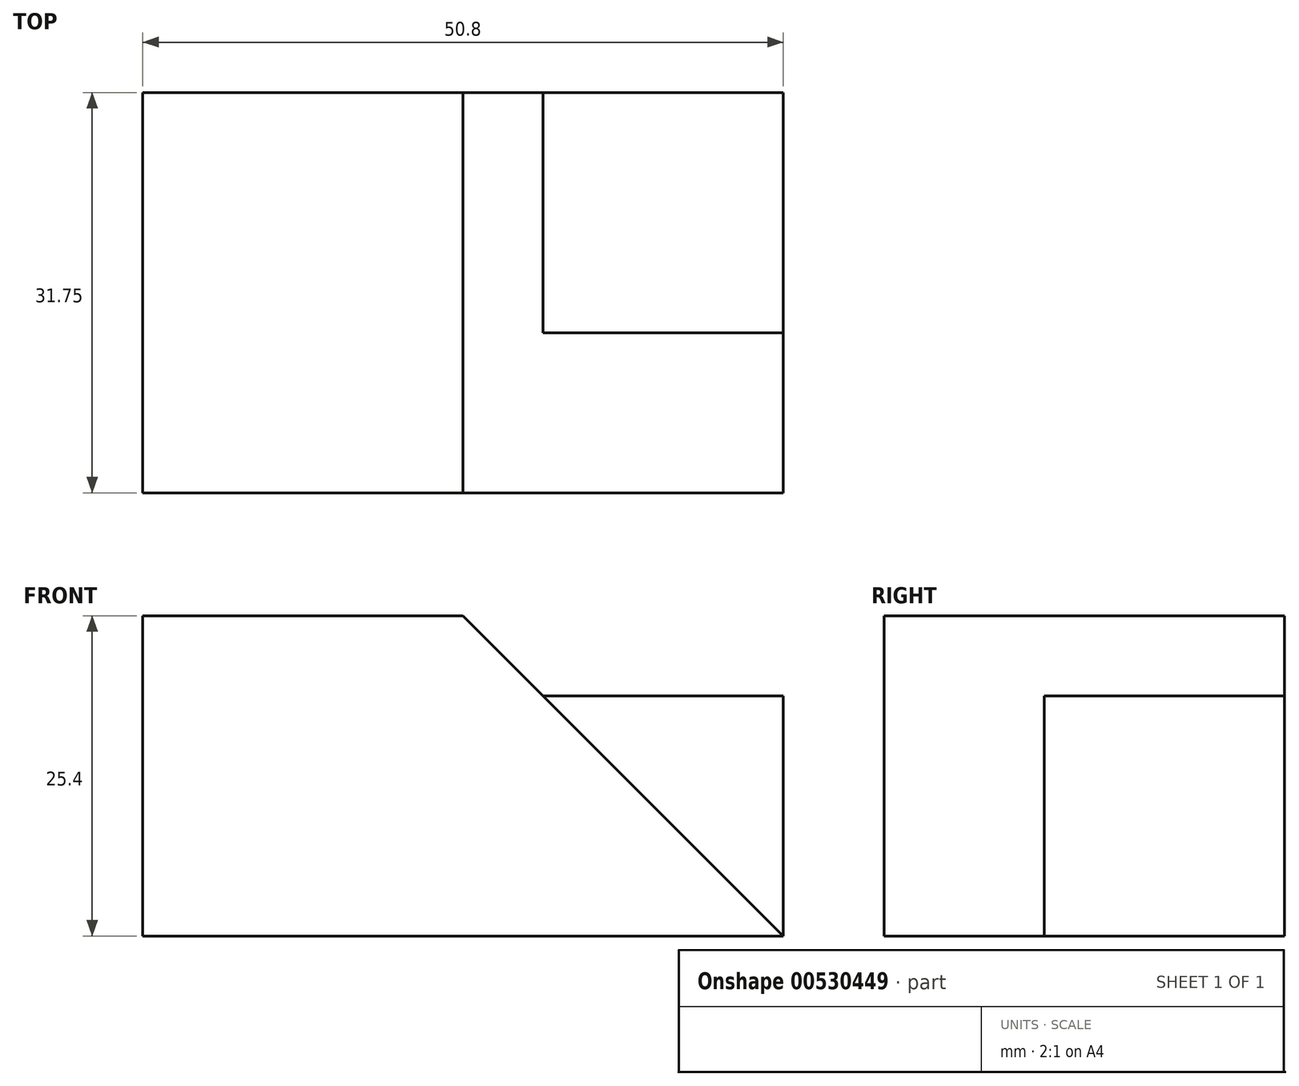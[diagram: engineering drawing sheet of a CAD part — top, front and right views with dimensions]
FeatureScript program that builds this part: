
annotation { "Feature Type Name" : "Feature", "Feature Type Description" : "" }
export const myFeature = defineFeature(function(context is Context, id is Id, definition is map)
    precondition{}
    {
        {
            var Q0;
            Q0=qCreatedBy(makeId("Front.planeOp"),FACE);
            var sketch = newSketch(context, id + "F0", { "sketchPlane" : qUnion([Q0])});
            skLineSegment(sketch, "E0", {"start": v(-56.42, 44.76) * mm, "end": v(-56.42, 19.36) * mm});
            skLineSegment(sketch, "E1", {"start": v(-56.42, 19.36) * mm, "end": v(-5.62, 19.36) * mm});
            skLineSegment(sketch, "E2", {"start": v(-5.62, 19.36) * mm, "end": v(-5.62, 44.76) * mm});
            skLineSegment(sketch, "E3", {"start": v(-5.62, 44.76) * mm, "end": v(-56.42, 44.76) * mm});
            skSolve(sketch);
        }
        {
            var Q0;
            Q0=makeQuery(id+"F0.imprint","IMPRINT",FACE,{"disambiguationData":[TD([[makeQuery(id+"F0.imprint","IMPRINT",EDGE,{"derivedFrom":sQuery(id+"F0.wireOp",EDGE,"E0")}),1.0]])]});
            extrude(context, id + "F1", {"entities" : qUnion([Q0]), "depth" : 31.75 * mm, "offsetDistance" : 25.4 * mm});
        }
        {
            var Q0;
            Q0=makeQuery(id+"F1.opExtrude","CAP_FACE",FACE,{"disambiguationData":[OSD([sQuery(id+"F0.wireOp",EDGE,"E0"),sQuery(id+"F0.wireOp",EDGE,"E1"),sQuery(id+"F0.wireOp",EDGE,"E2"),sQuery(id+"F0.wireOp",EDGE,"E3")])],"isStart":false});
            var sketch = newSketch(context, id + "F2", { "sketchPlane" : qUnion([Q0])});
            skLineSegment(sketch, "E4", {"start": v(-5.62, 19.36) * mm, "end": v(-24.67, 38.41) * mm});
            skLineSegment(sketch, "E5", {"start": v(-24.67, 38.41) * mm, "end": v(-5.62, 38.41) * mm});
            skLineSegment(sketch, "E6", {"start": v(-5.62, 38.41) * mm, "end": v(-5.62, 19.36) * mm});
            skLineSegment(sketch, "E7", {"start": v(-5.62, 19.36) * mm, "end": v(-31.02, 44.76) * mm});
            skLineSegment(sketch, "E8", {"start": v(-31.02, 44.76) * mm, "end": v(-5.62, 44.76) * mm});
            skLineSegment(sketch, "E9", {"start": v(-5.62, 44.76) * mm, "end": v(-5.62, 38.41) * mm});
            skLineSegment(sketch, "E10", {"start": v(-24.67, 38.41) * mm, "end": v(-31.02, 44.76) * mm});
            skSolve(sketch);
        }
        {
            var Q0;
            Q0=makeQuery(id+"F2.imprint","IMPRINT",FACE,{"disambiguationData":[TD([[makeQuery(id+"F2.imprint","IMPRINT",EDGE,{"derivedFrom":sQuery(id+"F2.wireOp",EDGE,"E5")}),-1.0]])]});
            extrude(context, id + "F3", {"entities" : qUnion([Q0]), "operationType" : NewBodyOperationType.REMOVE, "oppositeDirection" : true, "depth" : 12.7 * mm, "offsetDistance" : 25.4 * mm});
        }
        {
            var Q0;
            Q0=makeQuery(id+"F1.opExtrude","CAP_FACE",FACE,{"disambiguationData":[OSD([sQuery(id+"F0.wireOp",EDGE,"E0"),sQuery(id+"F0.wireOp",EDGE,"E1"),sQuery(id+"F0.wireOp",EDGE,"E2"),sQuery(id+"F0.wireOp",EDGE,"E3")])],"isStart":false});
            var sketch = newSketch(context, id + "F4", { "sketchPlane" : qUnion([Q0])});
            skLineSegment(sketch, "E11", {"start": v(-24.67, 38.41) * mm, "end": v(-31.02, 44.76) * mm});
            skLineSegment(sketch, "E12", {"start": v(-31.02, 44.76) * mm, "end": v(-5.62, 44.76) * mm});
            skLineSegment(sketch, "E13", {"start": v(-5.62, 44.76) * mm, "end": v(-5.62, 38.41) * mm});
            skLineSegment(sketch, "E14", {"start": v(-5.62, 38.41) * mm, "end": v(-24.67, 38.41) * mm});
            skSolve(sketch);
        }
        {
            var Q0;
            Q0 = qSketchRegion(id + "F4", true);
            extrude(context, id + "F5", {"entities" : qUnion([Q0]), "operationType" : NewBodyOperationType.REMOVE, "endBound" : BoundingType.THROUGH_ALL, "oppositeDirection" : true, "depth" : 25.4 * mm, "offsetDistance" : 25.4 * mm});
        }
    });
